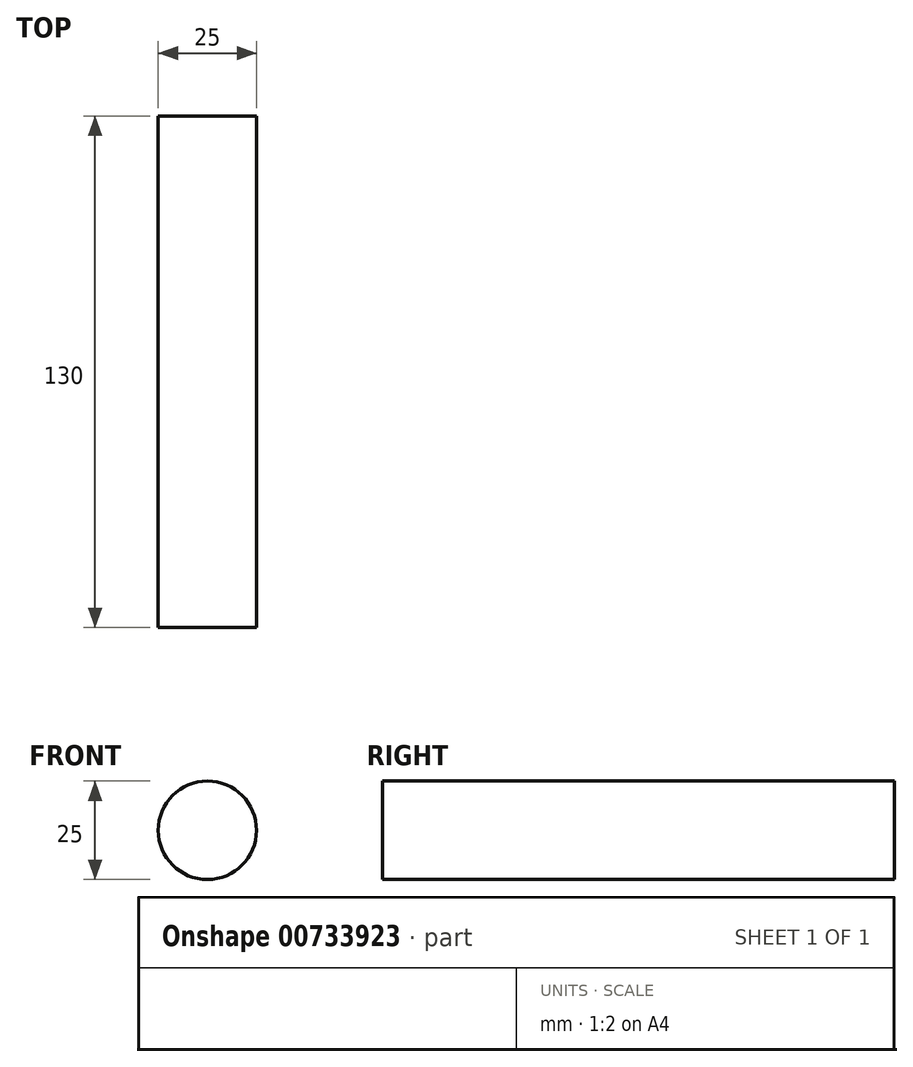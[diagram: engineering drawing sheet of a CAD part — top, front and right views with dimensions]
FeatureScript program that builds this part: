
annotation { "Feature Type Name" : "Feature", "Feature Type Description" : "" }
export const myFeature = defineFeature(function(context is Context, id is Id, definition is map)
    precondition{}
    {
        {
            var Q0;
            Q0=qCreatedBy(makeId("Front.planeOp"),FACE);
            var sketch = newSketch(context, id + "F0", { "sketchPlane" : qUnion([Q0])});
            skCircle(sketch, "E0", {"center": v(0, 0) * mm, "radius": 12.5 * mm});
            skSolve(sketch);
        }
        {
            var Q0;
            Q0=makeQuery(id+"F0.imprint","IMPRINT",FACE,{"disambiguationData":[TD([[makeQuery(id+"F0.imprint","IMPRINT",EDGE,{"derivedFrom":sQuery(id+"F0.wireOp",EDGE,"E0")}),1.0]])]});
            extrude(context, id + "F1", {"entities" : qUnion([Q0]), "depth" : 130 * mm, "offsetDistance" : 25 * mm});
        }
    });
